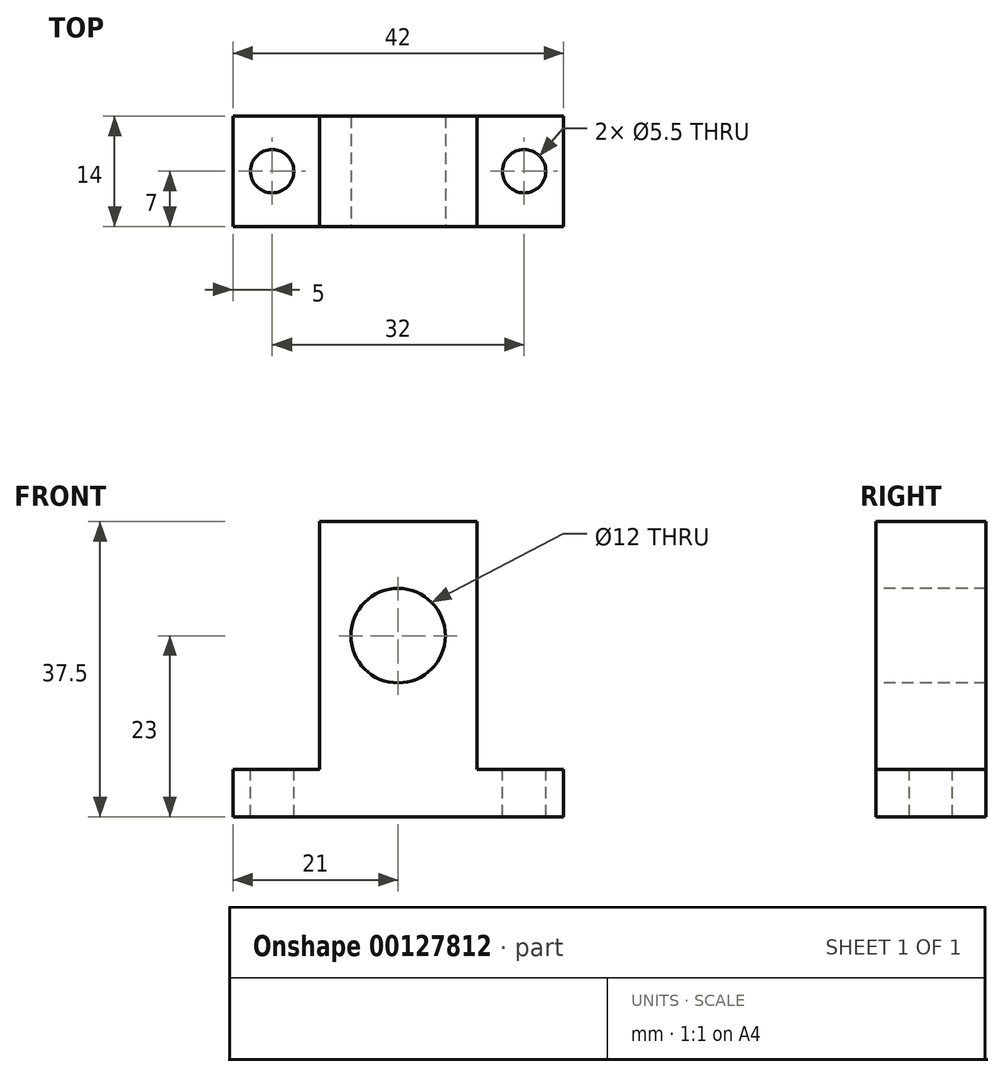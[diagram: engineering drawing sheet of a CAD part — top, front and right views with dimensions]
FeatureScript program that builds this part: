
annotation { "Feature Type Name" : "Feature", "Feature Type Description" : "" }
export const myFeature = defineFeature(function(context is Context, id is Id, definition is map)
    precondition{}
    {
        {
            var Q0;
            Q0=qCreatedBy(makeId("Front.planeOp"),FACE);
            var sketch = newSketch(context, id + "F0", { "sketchPlane" : qUnion([Q0])});
            skLineSegment(sketch, "E0", {"start": v(0, 0) * mm, "end": v(-21, 0) * mm});
            skLineSegment(sketch, "E1", {"start": v(-21, 0) * mm, "end": v(-21, 6) * mm});
            skLineSegment(sketch, "E2", {"start": v(-21, 6) * mm, "end": v(-10, 6) * mm});
            skLineSegment(sketch, "E3", {"start": v(-10, 6) * mm, "end": v(-10, 37.5) * mm});
            skLineSegment(sketch, "E4", {"start": v(-10, 37.5) * mm, "end": v(0, 37.5) * mm});
            skLineSegment(sketch, "E5", {"start": v(0, 0) * mm, "end": v(0, -16.95) * mm, "construction": true});
            skLineSegment(sketch, "E6.MirrorCS", {"start": v(10, 37.5) * mm, "end": v(0, 37.5) * mm});
            skLineSegment(sketch, "E7.MirrorCS", {"start": v(10, 6) * mm, "end": v(10, 37.5) * mm});
            skLineSegment(sketch, "E8.MirrorCS", {"start": v(21, 6) * mm, "end": v(10, 6) * mm});
            skLineSegment(sketch, "E9.MirrorCS", {"start": v(0, 0) * mm, "end": v(21, 0) * mm});
            skLineSegment(sketch, "E10.MirrorCS", {"start": v(21, 0) * mm, "end": v(21, 6) * mm});
            skSolve(sketch);
        }
        {
            var Q0;
            Q0 = qSketchRegion(id + "F0", true);
            extrude(context, id + "F1", {"entities" : qUnion([Q0]), "endBound" : BoundingType.SYMMETRIC, "depth" : 14 * mm});
        }
        {
            var Q0;
            Q0=makeQuery(id+"F1.opExtrude","CAP_FACE",FACE,{"disambiguationData":[OSD([sQuery(id+"F0.wireOp",EDGE,"E0"),sQuery(id+"F0.wireOp",EDGE,"E1"),sQuery(id+"F0.wireOp",EDGE,"E2"),sQuery(id+"F0.wireOp",EDGE,"E3"),sQuery(id+"F0.wireOp",EDGE,"E4"),sQuery(id+"F0.wireOp",EDGE,"E6.MirrorCS"),sQuery(id+"F0.wireOp",EDGE,"E7.MirrorCS"),sQuery(id+"F0.wireOp",EDGE,"E8.MirrorCS"),sQuery(id+"F0.wireOp",EDGE,"E9.MirrorCS"),sQuery(id+"F0.wireOp",EDGE,"E10.MirrorCS")])],"isStart":false});
            var sketch = newSketch(context, id + "F2", { "sketchPlane" : qUnion([Q0])});
            skCircle(sketch, "E11", {"center": v(0, 23) * mm, "radius": 6 * mm});
            skSolve(sketch);
        }
        {
            var Q0;
            Q0 = qSketchRegion(id + "F2", true);
            extrude(context, id + "F3", {"entities" : qUnion([Q0]), "operationType" : NewBodyOperationType.REMOVE, "endBound" : BoundingType.THROUGH_ALL, "oppositeDirection" : true, "depth" : 25 * mm});
        }
        {
            var Q0;
            Q0=makeQuery(id+"F1.opExtrude","SWEPT_FACE",FACE,{"disambiguationData":[OSD([sQuery(id+"F0.wireOp",EDGE,"E2")])]});
            var sketch = newSketch(context, id + "F4", { "sketchPlane" : qUnion([Q0])});
            skCircle(sketch, "E12", {"center": v(-16, 0) * mm, "radius": 2.75 * mm});
            skLineSegment(sketch, "E13", {"start": v(0, 0) * mm, "end": v(0, -22.2) * mm, "construction": true});
            skCircle(sketch, "E14.MirrorC", {"center": v(16, 0) * mm, "radius": 2.75 * mm});
            skSolve(sketch);
        }
        {
            var Q0;
            Q0 = qSketchRegion(id + "F4", true);
            extrude(context, id + "F5", {"entities" : qUnion([Q0]), "operationType" : NewBodyOperationType.REMOVE, "endBound" : BoundingType.THROUGH_ALL, "oppositeDirection" : true, "depth" : 25 * mm});
        }
    });
